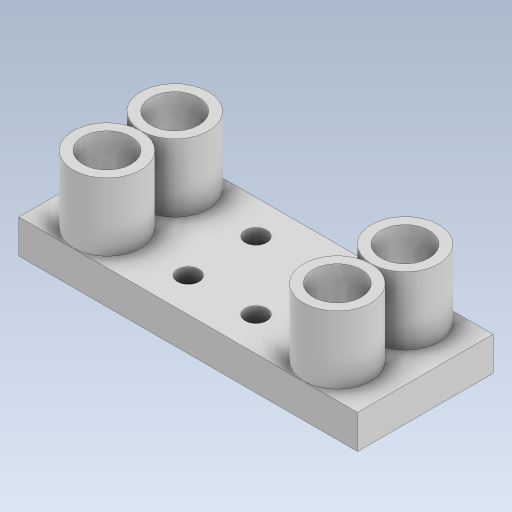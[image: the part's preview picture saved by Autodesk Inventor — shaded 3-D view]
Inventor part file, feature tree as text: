
AUTODESK INVENTOR PART (.ipt)
format: ipt  version: 2023.5 (Build 275446000, 446)  size: 183,296 bytes
history: native  units: mm
features: extrude x2, sketch x1
ambient origin geometry x8: Origin, YZ Plane, XZ Plane, XY Plane, X Axis, Y Axis, Z Axis, Center Point
bodies: Solid1 (feature_tree)
feature tree (3):
  sketch  "Sketch1"  dims[d0=50.0mm d1=20.0mm d2=7.1mm d3=5.0mm d4=3.2mm d5=12.0mm d6=10.0mm d7=10.0mm d8=10.0mm d9=10.0mm d10=5.0mm d11=0.0mm d12=15.0mm d13=0.0mm]
  extrude  "Extrusion1"  Depth=20.0mm
  extrude  "Extrusion2"  Depth=15.0mm
